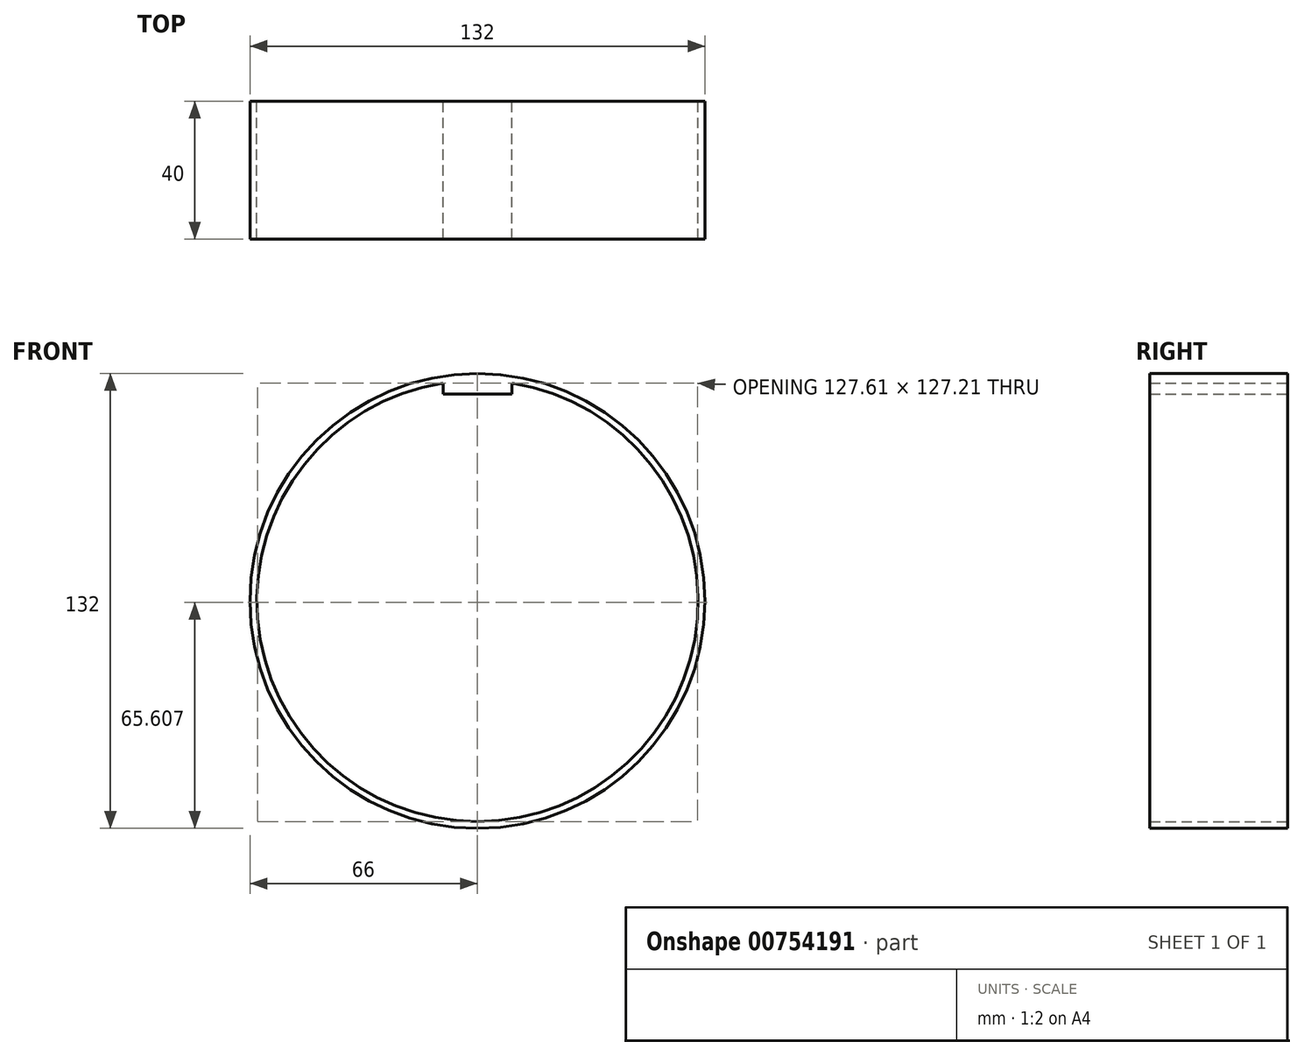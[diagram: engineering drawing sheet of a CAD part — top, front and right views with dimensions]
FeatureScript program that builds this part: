
annotation { "Feature Type Name" : "Feature", "Feature Type Description" : "" }
export const myFeature = defineFeature(function(context is Context, id is Id, definition is map)
    precondition{}
    {
        {
            var Q0;
            Q0=qCreatedBy(makeId("Front.planeOp"),FACE);
            var sketch = newSketch(context, id + "F0", { "sketchPlane" : qUnion([Q0])});
            skCircle(sketch, "E0", {"center": v(0, 0) * mm, "radius": 66 * mm});
            skLineSegment(sketch, "E1", {"start": v(0, 0) * mm, "end": v(8.04, 45.6) * mm});
            skLineSegment(sketch, "E2.MirrorCS", {"start": v(0, 0) * mm, "end": v(-8.04, 45.6) * mm});
            skArc(sketch, "E3", {"start": v(-10, 63.21) * mm, "mid": v(0, -64) * mm, "end": v(10, 63.21) * mm});
            skLineSegment(sketch, "E4", {"start": v(10, 60) * mm, "end": v(10, 63.21) * mm});
            skLineSegment(sketch, "E5.MirrorCS", {"start": v(-10, 60) * mm, "end": v(-10, 63.21) * mm});
            skLineSegment(sketch, "E6", {"start": v(-10, 60) * mm, "end": v(10, 60) * mm});
            skLineSegment(sketch, "E7", {"start": v(0, 0) * mm, "end": v(0, 31.3) * mm});
            skSolve(sketch);
        }
        {
            var Q0;
            Q0=makeQuery(id+"F0.imprint","IMPRINT",FACE,{"disambiguationData":[TD([[makeQuery(id+"F0.imprint","IMPRINT",EDGE,{"derivedFrom":sQuery(id+"F0.wireOp",EDGE,"E0")}),1.0]])]});
            extrude(context, id + "F1", {"entities" : qUnion([Q0]), "depth" : 40 * mm, "offsetDistance" : 25 * mm});
        }
    });
